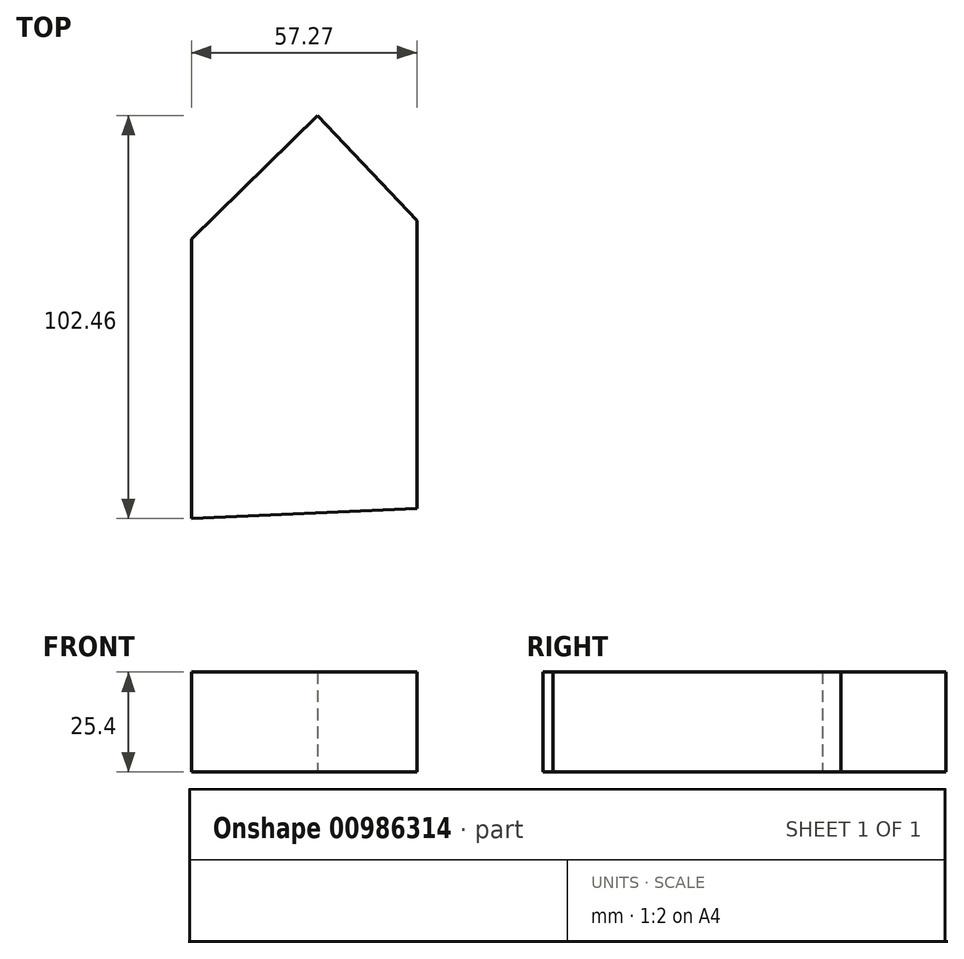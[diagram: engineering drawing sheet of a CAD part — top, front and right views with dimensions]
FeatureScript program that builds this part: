
annotation { "Feature Type Name" : "Feature", "Feature Type Description" : "" }
export const myFeature = defineFeature(function(context is Context, id is Id, definition is map)
    precondition{}
    {
        {
            var Q0;
            Q0=qCreatedBy(makeId("Top.planeOp"),FACE);
            var sketch = newSketch(context, id + "F0", { "sketchPlane" : qUnion([Q0])});
            skLineSegment(sketch, "E0", {"start": v(-32.05, 26.9) * mm, "end": v(-32.05, -44.18) * mm});
            skLineSegment(sketch, "E1", {"start": v(-32.05, -44.18) * mm, "end": v(25.22, -41.59) * mm});
            skLineSegment(sketch, "E2", {"start": v(25.22, -41.59) * mm, "end": v(25.22, 31.51) * mm});
            skLineSegment(sketch, "E3", {"start": v(25.22, 31.51) * mm, "end": v(0, 58.28) * mm});
            skLineSegment(sketch, "E4", {"start": v(0, 58.28) * mm, "end": v(-32.05, 26.9) * mm});
            skSolve(sketch);
        }
        {
            var Q0;
            Q0 = qSketchRegion(id + "F0", true);
            extrude(context, id + "F1", {"entities" : qUnion([Q0]), "depth" : 25.4 * mm, "offsetDistance" : 25.4 * mm});
        }
    });
